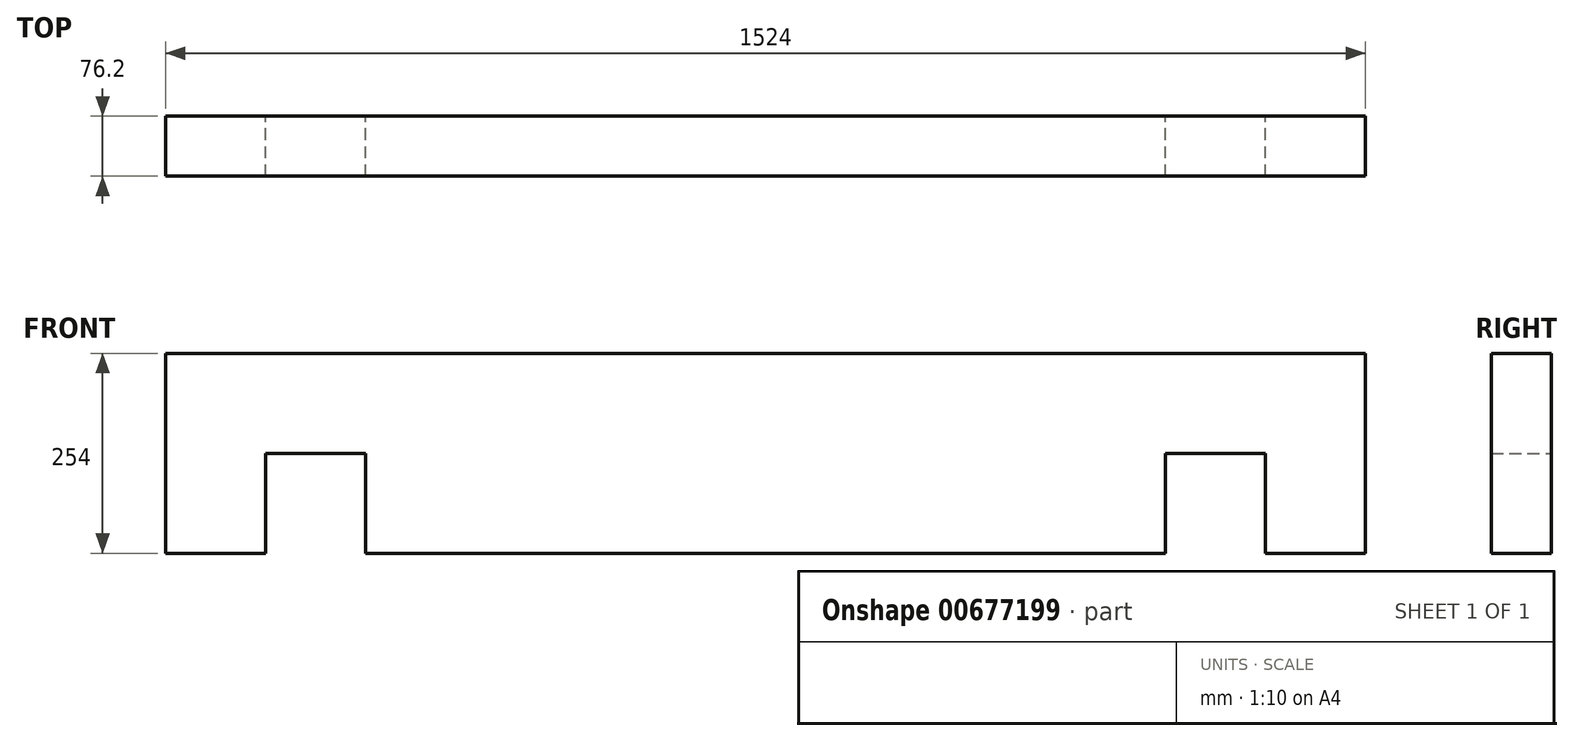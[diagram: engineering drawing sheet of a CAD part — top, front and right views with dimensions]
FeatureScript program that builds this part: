
annotation { "Feature Type Name" : "Feature", "Feature Type Description" : "" }
export const myFeature = defineFeature(function(context is Context, id is Id, definition is map)
    precondition{}
    {
        {
            var Q0;
            Q0=qCreatedBy(makeId("Front.planeOp"),FACE);
            var sketch = newSketch(context, id + "F0", { "sketchPlane" : qUnion([Q0])});
            skLineSegment(sketch, "E0.bottom", {"start": v(-762, -127) * mm, "end": v(-635, -127) * mm});
            skLineSegment(sketch, "E0.top", {"start": v(-762, 127) * mm, "end": v(762, 127) * mm});
            skLineSegment(sketch, "E0.left", {"start": v(-762, -127) * mm, "end": v(-762, 127) * mm});
            skLineSegment(sketch, "E0.right", {"start": v(762, -127) * mm, "end": v(762, 127) * mm});
            skPoint(sketch, "E0.middle", {"position": v(0, 0) * mm});
            skLineSegment(sketch, "E1.top", {"start": v(-635, 0) * mm, "end": v(-508, 0) * mm});
            skLineSegment(sketch, "E1.left", {"start": v(-635, -127) * mm, "end": v(-635, 0) * mm});
            skLineSegment(sketch, "E1.right", {"start": v(-508, -127) * mm, "end": v(-508, 0) * mm});
            skLineSegment(sketch, "E2.trimOffspring", {"start": v(-508, -127) * mm, "end": v(508, -127) * mm});
            skLineSegment(sketch, "E3.top", {"start": v(635, 0) * mm, "end": v(508, 0) * mm});
            skLineSegment(sketch, "E3.left", {"start": v(635, -127) * mm, "end": v(635, 0) * mm});
            skLineSegment(sketch, "E3.right", {"start": v(508, -127) * mm, "end": v(508, 0) * mm});
            skLineSegment(sketch, "E4.trimOffspring", {"start": v(635, -127) * mm, "end": v(762, -127) * mm});
            skSolve(sketch);
        }
        {
            var Q0;
            Q0 = qSketchRegion(id + "F0", true);
            extrude(context, id + "F1", {"entities" : qUnion([Q0]), "depth" : 76.2 * mm, "offsetDistance" : 25.4 * mm});
        }
    });
